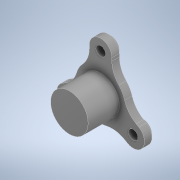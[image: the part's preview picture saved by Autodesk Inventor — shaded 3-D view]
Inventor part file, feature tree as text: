
AUTODESK INVENTOR PART (.ipt)
format: ipt  version: 2022 (Build 260153000, 153)  size: 163,328 bytes
history: mixed  units: in
note: dims shown in document units (in); Inventor stores cm internally (conversion verified against a paired STEP export)
features: extrude x3, sketch x3, chamfer x1, imported_body x1
ambient origin geometry x8: Origin, YZ Plane, XZ Plane, XY Plane, X Axis, Y Axis, Z Axis, Center Point
bodies: Solid1 (imported_parasolid)
feature tree (8):
  extrude  "Extrusion4"  Depth=0.3937in TaperAngle=0.0deg
  extrude  "Extrusion5"  Depth=0.4921in TaperAngle=0.0deg
  extrude  "Extrusion6"  [1 undecoded]
  sketch  "Sketch4"  dims[d8=0.0in d9=0.0in d10=0.3937in d11=0.0in]
  sketch  "Sketch5"  dims[d12=0.5906in d13=0.4921in d14=0.0in]
  sketch  "Sketch6"
  chamfer  "Chamfer5"  [1 undecoded]
  imported_body  NMx_Import_Brep_tag  [imported B-rep: ~31 faces, bbox_mm=[31.788121, 26.496463, 16.5]]
note: 2 required parameter values undecoded (feature->parameter linkage not recoverable at this tier; creation-order binding heuristic only, values carry confidence <= 0.55)
